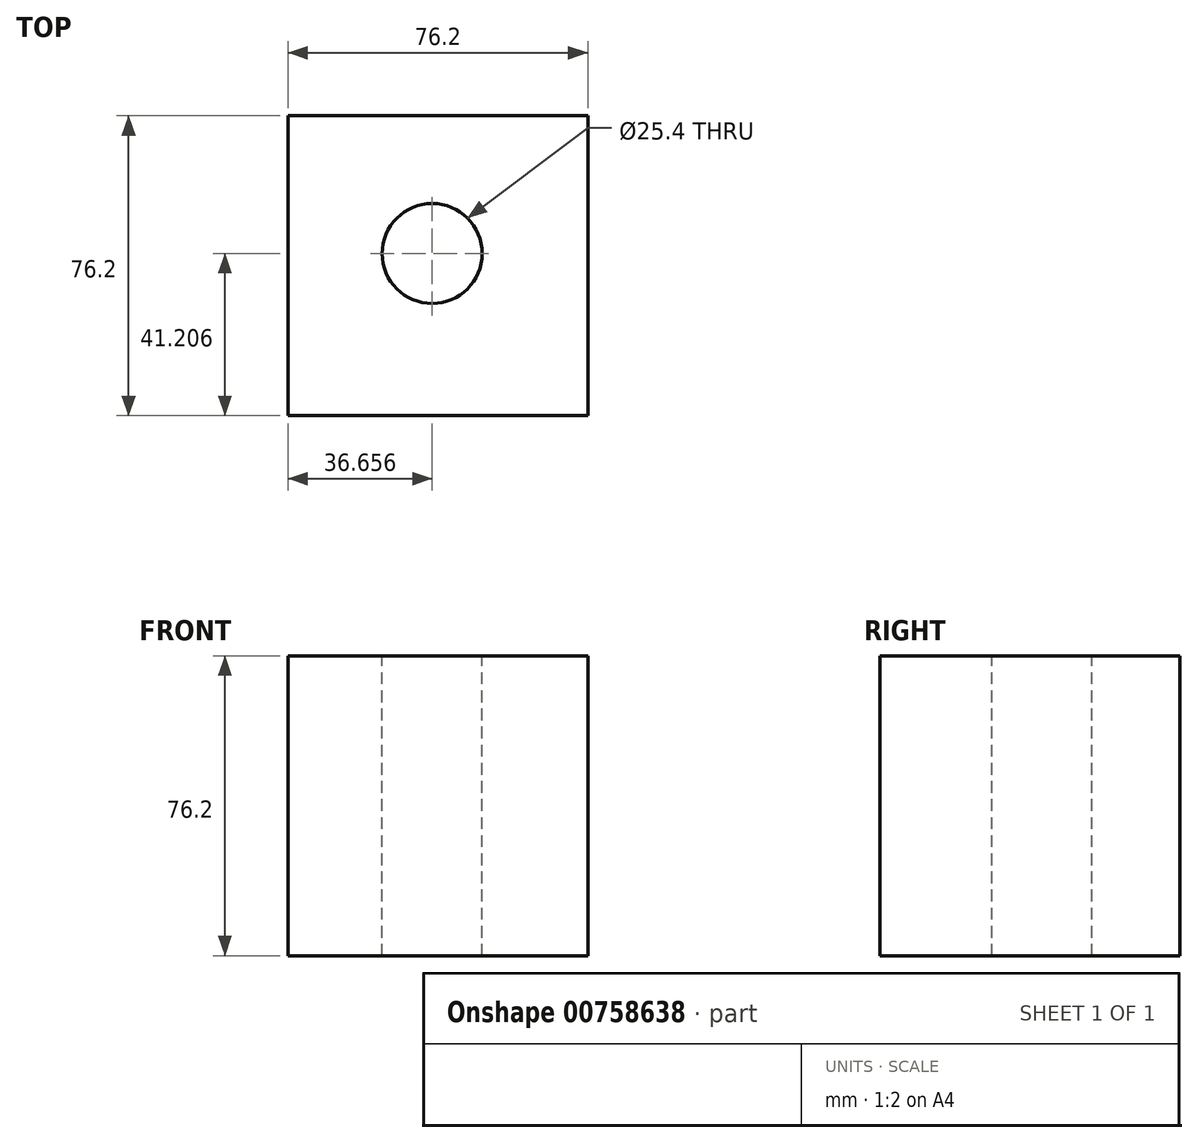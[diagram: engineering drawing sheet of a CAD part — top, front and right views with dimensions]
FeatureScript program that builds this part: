
annotation { "Feature Type Name" : "Feature", "Feature Type Description" : "" }
export const myFeature = defineFeature(function(context is Context, id is Id, definition is map)
    precondition{}
    {
        {
            var Q0;
            Q0=qCreatedBy(makeId("Front.planeOp"),FACE);
            var sketch = newSketch(context, id + "F0", { "sketchPlane" : qUnion([Q0])});
            skLineSegment(sketch, "E0.bottom", {"start": v(-39.43, 45.72) * mm, "end": v(36.77, 45.72) * mm});
            skLineSegment(sketch, "E0.top", {"start": v(-39.43, -30.48) * mm, "end": v(36.77, -30.48) * mm});
            skLineSegment(sketch, "E0.left", {"start": v(-39.43, 45.72) * mm, "end": v(-39.43, -30.48) * mm});
            skLineSegment(sketch, "E0.right", {"start": v(36.77, 45.72) * mm, "end": v(36.77, -30.48) * mm});
            skSolve(sketch);
        }
        {
            var Q0;
            Q0=makeQuery(id+"F0.imprint","IMPRINT",FACE,{"disambiguationData":[TD([[makeQuery(id+"F0.imprint","IMPRINT",EDGE,{"derivedFrom":sQuery(id+"F0.wireOp",EDGE,"E0.bottom")}),-1.0]])]});
            extrude(context, id + "F1", {"entities" : qUnion([Q0]), "depth" : 76.2 * mm, "offsetDistance" : 25.4 * mm});
        }
        {
            var Q0;
            Q0=makeQuery(id+"F1.opExtrude","CAP_FACE",FACE,{"disambiguationData":[OSD([sQuery(id+"F0.wireOp",EDGE,"E0.bottom"),sQuery(id+"F0.wireOp",EDGE,"E0.top"),sQuery(id+"F0.wireOp",EDGE,"E0.left"),sQuery(id+"F0.wireOp",EDGE,"E0.right")])],"isStart":false});
            var sketch = newSketch(context, id + "F2", { "sketchPlane" : qUnion([Q0])});
            skLineSegment(sketch, "E1.bottom", {"start": v(-14.03, -5.08) * mm, "end": v(11.37, -5.08) * mm});
            skLineSegment(sketch, "E1.top", {"start": v(-14.03, 20.32) * mm, "end": v(11.37, 20.32) * mm});
            skLineSegment(sketch, "E1.left", {"start": v(-14.03, -5.08) * mm, "end": v(-14.03, 20.32) * mm});
            skLineSegment(sketch, "E1.right", {"start": v(11.37, -5.08) * mm, "end": v(11.37, 20.32) * mm});
            skLineSegment(sketch, "E2.bottom", {"start": v(-11.04, 15.34) * mm, "end": v(9.53, 15.34) * mm});
            skLineSegment(sketch, "E2.top", {"start": v(-11.04, -0.68) * mm, "end": v(9.53, -0.68) * mm});
            skLineSegment(sketch, "E2.left", {"start": v(-11.04, 15.34) * mm, "end": v(-11.04, -0.68) * mm});
            skLineSegment(sketch, "E2.right", {"start": v(9.53, 15.34) * mm, "end": v(9.53, -0.68) * mm});
            skLineSegment(sketch, "E3.bottom", {"start": v(-7.92, 11.93) * mm, "end": v(6.3, 11.93) * mm});
            skLineSegment(sketch, "E3.top", {"start": v(-7.92, 2.07) * mm, "end": v(6.3, 2.07) * mm});
            skLineSegment(sketch, "E3.left", {"start": v(-7.92, 11.93) * mm, "end": v(-7.92, 2.07) * mm});
            skLineSegment(sketch, "E3.right", {"start": v(6.3, 11.93) * mm, "end": v(6.3, 2.07) * mm});
            skLineSegment(sketch, "E4.bottom", {"start": v(-5.45, 9.09) * mm, "end": v(4.4, 9.09) * mm});
            skLineSegment(sketch, "E4.top", {"start": v(-5.45, 3.97) * mm, "end": v(4.4, 3.97) * mm});
            skLineSegment(sketch, "E4.left", {"start": v(-5.45, 9.09) * mm, "end": v(-5.45, 3.97) * mm});
            skLineSegment(sketch, "E4.right", {"start": v(4.4, 9.09) * mm, "end": v(4.4, 3.97) * mm});
            skSolve(sketch);
        }
        {
            var Q0;
            Q0=makeQuery(id+"F2.imprint","IMPRINT",FACE,{"disambiguationData":[TD([[makeQuery(id+"F2.imprint","IMPRINT",EDGE,{"derivedFrom":sQuery(id+"F2.wireOp",EDGE,"E1.bottom")}),1.0]])]});
            var Q1;
            Q1=sQuery(id+"F2.wireOp",EDGE,"E1.right");
            var Q2;
            Q2=sQuery(id+"F2.wireOp",EDGE,"E1.top");
            var Q3;
            Q3=sQuery(id+"F2.wireOp",EDGE,"E1.left");
            var Q4;
            Q4=sQuery(id+"F2.wireOp",EDGE,"E1.bottom");
            var Q5;
            Q5=sQuery(id+"F2.wireOp",EDGE,"E2.bottom");
            var Q6;
            Q6=sQuery(id+"F2.wireOp",EDGE,"E2.left");
            var Q7;
            Q7=sQuery(id+"F2.wireOp",EDGE,"E3.left");
            var Q8;
            Q8=sQuery(id+"F2.wireOp",EDGE,"E3.bottom");
            var Q9;
            Q9=sQuery(id+"F2.wireOp",EDGE,"E4.bottom");
            var Q10;
            Q10=sQuery(id+"F2.wireOp",EDGE,"E4.left");
            var Q11;
            Q11=sQuery(id+"F2.wireOp",EDGE,"E2.top");
            var Q12;
            Q12=sQuery(id+"F2.wireOp",EDGE,"E3.top");
            var Q13;
            Q13=sQuery(id+"F2.wireOp",EDGE,"E4.top");
            var Q14;
            Q14=sQuery(id+"F2.wireOp",EDGE,"E4.right");
            var Q15;
            Q15=sQuery(id+"F2.wireOp",EDGE,"E3.right");
            var Q16;
            Q16=sQuery(id+"F2.wireOp",EDGE,"E2.right");
            extrude(context, id + "F3", {"entities" : qUnion([Q0]), "bodyType" : ToolBodyType.SURFACE, "operationType" : NewBodyOperationType.ADD, "surfaceEntities" : qUnion([Q1, Q2, Q3, Q4, Q5, Q6, Q7, Q8, Q9, Q10, Q11, Q12, Q13, Q14, Q15, Q16]), "depth" : 12.7 * mm, "offsetDistance" : 25.4 * mm});
        }
        {
            var Q0;
            Q0=makeQuery(id+"F1.opExtrude","SWEPT_FACE",FACE,{"disambiguationData":[OSD([sQuery(id+"F0.wireOp",EDGE,"E0.right")])]});
            var sketch = newSketch(context, id + "F4", { "sketchPlane" : qUnion([Q0])});
            skCircle(sketch, "E5", {"center": v(-38.1, 7.62) * mm, "radius": 12.9 * mm});
            skCircle(sketch, "E6", {"center": v(-38.1, 7.62) * mm, "radius": 8.98 * mm});
            skCircle(sketch, "E7", {"center": v(-38.1, 7.62) * mm, "radius": 5.36 * mm});
            skCircle(sketch, "E8", {"center": v(-38.1, 7.62) * mm, "radius": 2.75 * mm});
            skSolve(sketch);
        }
        {
            var Q0;
            Q0=makeQuery(id+"F4.imprint","IMPRINT",FACE,{"disambiguationData":[TD([[makeQuery(id+"F4.imprint","IMPRINT",EDGE,{"derivedFrom":sQuery(id+"F4.wireOp",EDGE,"E5")}),1.0]])]});
            var Q1;
            Q1=sQuery(id+"F4.wireOp",EDGE,"E5");
            var Q2;
            Q2=sQuery(id+"F4.wireOp",EDGE,"E6");
            var Q3;
            Q3=sQuery(id+"F4.wireOp",EDGE,"E7");
            var Q4;
            Q4=sQuery(id+"F4.wireOp",EDGE,"E8");
            extrude(context, id + "F5", {"entities" : qUnion([Q0]), "bodyType" : ToolBodyType.SURFACE, "operationType" : NewBodyOperationType.ADD, "surfaceEntities" : qUnion([Q1, Q2, Q3, Q4]), "depth" : 12.7 * mm, "offsetDistance" : 25.4 * mm});
        }
        {
            var Q0;
            Q0=makeQuery(id+"F1.opExtrude","SWEPT_FACE",FACE,{"disambiguationData":[OSD([sQuery(id+"F0.wireOp",EDGE,"E0.bottom")])]});
            var sketch = newSketch(context, id + "F6", { "sketchPlane" : qUnion([Q0])});
            skPoint(sketch, "E9", {"position": v(-2.77, -35) * mm});
            skSolve(sketch);
        }
        {
            var Q0;
            Q0=sQuery(id+"F6.wireOp",VERTEX,"E9");
            var Q1;
            Q1=makeQuery(id+"F1.opExtrude","SWEPT_BODY",BODY,{"disambiguationData":[OSD([sQuery(id+"F0.wireOp",EDGE,"E0.bottom"),sQuery(id+"F0.wireOp",EDGE,"E0.top"),sQuery(id+"F0.wireOp",EDGE,"E0.left"),sQuery(id+"F0.wireOp",EDGE,"E0.right")])]});
            hole(context, id + "F7", {"style" : HoleStyle.SIMPLE, "endStyle" : HoleEndStyle.THROUGH, "holeDiameter" : 25.4 * mm, "majorDiameter" : 6.35 * mm, "isTappedThrough" : true, "tappedDepth" : 12.7 * mm, "tapClearance" : 3, "locations" : qUnion([Q0]), "scope" : qUnion([Q1])});
        }
        {
            var Q0;
            Q0=makeQuery(id+"F1.opExtrude","SWEPT_FACE",FACE,{"disambiguationData":[OSD([sQuery(id+"F0.wireOp",EDGE,"E0.left")])]});
            var sketch = newSketch(context, id + "F8", { "sketchPlane" : qUnion([Q0])});
            skCircle(sketch, "E10.cCircle", {"center": v(35.59, 10.6) * mm, "radius": 24.94 * mm, "construction": true});
            skLineSegment(sketch, "E10.0", {"start": v(47.95, 38.84) * mm, "end": v(66.27, 7.58) * mm});
            skLineSegment(sketch, "E10.1", {"start": v(66.27, 7.58) * mm, "end": v(42.19, -19.51) * mm});
            skLineSegment(sketch, "E10.2", {"start": v(42.19, -19.51) * mm, "end": v(8.99, -4.98) * mm});
            skLineSegment(sketch, "E10.3", {"start": v(8.99, -4.98) * mm, "end": v(12.54, 31.08) * mm});
            skLineSegment(sketch, "E10.4", {"start": v(12.54, 31.08) * mm, "end": v(47.95, 38.84) * mm});
            skPoint(sketch, "E10.0.midPoint", {"position": v(57.1, 23.21) * mm});
            skCircle(sketch, "E11.cCircle", {"center": v(35.59, 10.6) * mm, "radius": 19.32 * mm, "construction": true});
            skLineSegment(sketch, "E11.0", {"start": v(42.1, 31.93) * mm, "end": v(57.32, 15.62) * mm});
            skLineSegment(sketch, "E11.1", {"start": v(57.32, 15.62) * mm, "end": v(50.8, -5.7) * mm});
            skLineSegment(sketch, "E11.2", {"start": v(50.8, -5.7) * mm, "end": v(29.07, -10.73) * mm});
            skLineSegment(sketch, "E11.3", {"start": v(29.07, -10.73) * mm, "end": v(13.85, 5.58) * mm});
            skLineSegment(sketch, "E11.4", {"start": v(13.85, 5.58) * mm, "end": v(20.37, 26.91) * mm});
            skLineSegment(sketch, "E11.5", {"start": v(20.37, 26.91) * mm, "end": v(42.1, 31.93) * mm});
            skPoint(sketch, "E11.0.midPoint", {"position": v(49.71, 23.78) * mm});
            skCircle(sketch, "E12.cCircle", {"center": v(35.59, 10.6) * mm, "radius": 14.01 * mm, "construction": true});
            skLineSegment(sketch, "E12.0", {"start": v(40.15, 26.13) * mm, "end": v(51.31, 14.41) * mm});
            skLineSegment(sketch, "E12.1", {"start": v(51.31, 14.41) * mm, "end": v(46.75, -1.11) * mm});
            skLineSegment(sketch, "E12.2", {"start": v(46.75, -1.11) * mm, "end": v(31.02, -4.92) * mm});
            skLineSegment(sketch, "E12.3", {"start": v(31.02, -4.92) * mm, "end": v(19.86, 6.79) * mm});
            skLineSegment(sketch, "E12.4", {"start": v(19.86, 6.79) * mm, "end": v(24.42, 22.32) * mm});
            skLineSegment(sketch, "E12.5", {"start": v(24.42, 22.32) * mm, "end": v(40.15, 26.13) * mm});
            skPoint(sketch, "E12.0.midPoint", {"position": v(45.73, 20.27) * mm});
            skCircle(sketch, "E13.cCircle", {"center": v(35.59, 10.6) * mm, "radius": 9.45 * mm, "construction": true});
            skLineSegment(sketch, "E13.0", {"start": v(38.64, 21.08) * mm, "end": v(46.19, 13.2) * mm});
            skLineSegment(sketch, "E13.1", {"start": v(46.19, 13.2) * mm, "end": v(43.14, 2.72) * mm});
            skLineSegment(sketch, "E13.2", {"start": v(43.14, 2.72) * mm, "end": v(32.54, 0.12) * mm});
            skLineSegment(sketch, "E13.3", {"start": v(32.54, 0.12) * mm, "end": v(24.98, 8) * mm});
            skLineSegment(sketch, "E13.4", {"start": v(24.98, 8) * mm, "end": v(28.03, 18.49) * mm});
            skLineSegment(sketch, "E13.5", {"start": v(28.03, 18.49) * mm, "end": v(38.64, 21.08) * mm});
            skPoint(sketch, "E13.0.midPoint", {"position": v(42.41, 17.14) * mm});
            skSolve(sketch);
        }
        {
            var Q0;
            Q0=sQuery(id+"F8.wireOp",EDGE,"E10.4");
            var Q1;
            Q1=sQuery(id+"F8.wireOp",EDGE,"E10.3");
            var Q2;
            Q2=sQuery(id+"F8.wireOp",EDGE,"E10.2");
            var Q3;
            Q3=sQuery(id+"F8.wireOp",EDGE,"E10.1");
            var Q4;
            Q4=sQuery(id+"F8.wireOp",EDGE,"E10.0");
            var Q5;
            Q5=sQuery(id+"F8.wireOp",EDGE,"E11.4");
            var Q6;
            Q6=sQuery(id+"F8.wireOp",EDGE,"E11.5");
            var Q7;
            Q7=sQuery(id+"F8.wireOp",EDGE,"E12.5");
            var Q8;
            Q8=sQuery(id+"F8.wireOp",EDGE,"E12.4");
            var Q9;
            Q9=sQuery(id+"F8.wireOp",EDGE,"E12.0");
            var Q10;
            Q10=sQuery(id+"F8.wireOp",EDGE,"E11.0");
            var Q11;
            Q11=sQuery(id+"F8.wireOp",EDGE,"E13.0");
            var Q12;
            Q12=sQuery(id+"F8.wireOp",EDGE,"E13.5");
            var Q13;
            Q13=sQuery(id+"F8.wireOp",EDGE,"E13.4");
            var Q14;
            Q14=sQuery(id+"F8.wireOp",EDGE,"E12.3");
            var Q15;
            Q15=sQuery(id+"F8.wireOp",EDGE,"E11.3");
            var Q16;
            Q16=sQuery(id+"F8.wireOp",EDGE,"E11.2");
            var Q17;
            Q17=sQuery(id+"F8.wireOp",EDGE,"E11.1");
            var Q18;
            Q18=sQuery(id+"F8.wireOp",EDGE,"E12.2");
            var Q19;
            Q19=sQuery(id+"F8.wireOp",EDGE,"E12.1");
            var Q20;
            Q20=sQuery(id+"F8.wireOp",EDGE,"E13.2");
            var Q21;
            Q21=sQuery(id+"F8.wireOp",EDGE,"E13.1");
            var Q22;
            Q22=sQuery(id+"F8.wireOp",EDGE,"E13.3");
            extrude(context, id + "F9", {"bodyType" : ToolBodyType.SURFACE, "operationType" : NewBodyOperationType.ADD, "surfaceEntities" : qUnion([Q0, Q1, Q2, Q3, Q4, Q5, Q6, Q7, Q8, Q9, Q10, Q11, Q12, Q13, Q14, Q15, Q16, Q17, Q18, Q19, Q20, Q21, Q22]), "depth" : 12.7 * mm, "offsetDistance" : 25.4 * mm});
        }
        {
            var Q0;
            Q0=makeQuery(id+"F1.opExtrude","CAP_FACE",FACE,{"disambiguationData":[OSD([sQuery(id+"F0.wireOp",EDGE,"E0.bottom"),sQuery(id+"F0.wireOp",EDGE,"E0.top"),sQuery(id+"F0.wireOp",EDGE,"E0.left"),sQuery(id+"F0.wireOp",EDGE,"E0.right")])],"isStart":true});
            var sketch = newSketch(context, id + "F10", { "sketchPlane" : qUnion([Q0])});
            skText(sketch, "E14", { "text": "Izzy", "fontName": "OpenSans-Regular.ttf"});
            const initialGuessF10  = {"E14": [-0.02545, -0.00295, 1, 0, 0.02474]};
            skSetInitialGuess(sketch, initialGuessF10);
            skSolve(sketch);
        }
        {
            var Q0;
            Q0=makeQuery(id+"F10.imprint","IMPRINT",FACE,{"disambiguationData":[TD([[makeQuery(id+"F10.imprint","IMPRINT",EDGE,{"derivedFrom":sQuery(id+"F10.wireOp",EDGE,"E14.sketch_text.stroke-0")}),1.0]])]});
            var Q1;
            Q1 = qConstructionFilter(qBodyType(qCreatedBy(id + "F10" ,EDGE), BodyType.WIRE), ConstructionObject.NO);
            extrude(context, id + "F11", {"entities" : qUnion([Q0]), "bodyType" : ToolBodyType.SURFACE, "operationType" : NewBodyOperationType.ADD, "surfaceEntities" : qUnion([Q1]), "depth" : 12.7 * mm, "offsetDistance" : 25.4 * mm});
        }
    });
